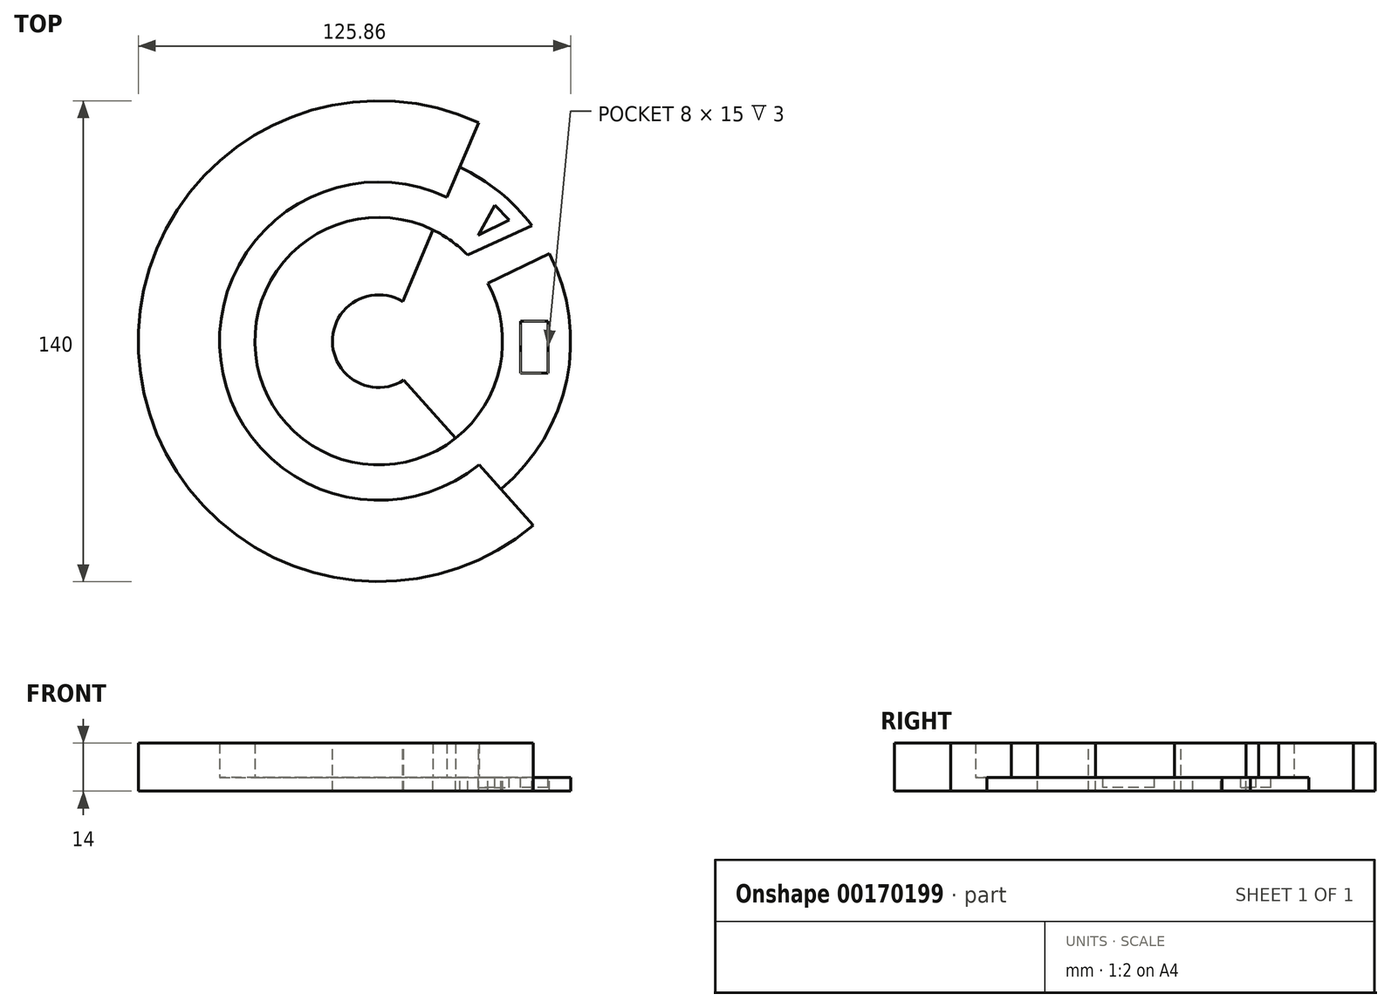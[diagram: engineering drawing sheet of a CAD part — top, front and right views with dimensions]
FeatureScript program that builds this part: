
annotation { "Feature Type Name" : "Feature", "Feature Type Description" : "" }
export const myFeature = defineFeature(function(context is Context, id is Id, definition is map)
    precondition{}
    {
        {
            var Q0;
            Q0=qCreatedBy(makeId("Top.planeOp"),FACE);
            var sketch = newSketch(context, id + "F0", { "sketchPlane" : qUnion([Q0])});
            skCircle(sketch, "E0", {"center": v(0, 0) * mm, "radius": 70 * mm});
            skCircle(sketch, "E1", {"center": v(0, 0) * mm, "radius": 46.34 * mm});
            skCircle(sketch, "E2", {"center": v(0, 0) * mm, "radius": 36.04 * mm});
            skCircle(sketch, "E3", {"center": v(0, 0) * mm, "radius": 13.49 * mm});
            skLineSegment(sketch, "E4", {"start": v(7.26, -11.37) * mm, "end": v(45, -53.62) * mm});
            skLineSegment(sketch, "E5", {"start": v(6.97, 11.55) * mm, "end": v(29.14, 63.65) * mm});
            skCircle(sketch, "E6", {"center": v(0, 0) * mm, "radius": 55.86 * mm});
            skCircle(sketch, "E7", {"center": v(0, 0) * mm, "radius": 32.82 * mm});
            skCircle(sketch, "E8", {"center": v(0, 0) * mm, "radius": 74.95 * mm});
            skLineSegment(sketch, "E9", {"start": v(26.8, -18.95) * mm, "end": v(42.53, -36.22) * mm});
            skLineSegment(sketch, "E10", {"start": v(49.72, 25.46) * mm, "end": v(28.92, 15.51) * mm});
            skLineSegment(sketch, "E11", {"start": v(22.75, 23.65) * mm, "end": v(40.37, 63.15) * mm});
            skLineSegment(sketch, "E12", {"start": v(22.75, 23.65) * mm, "end": v(62.3, 41.68) * mm});
            skSolve(sketch);
        }
        {
            var Q0;
            {var subQ0=sQuery(id+"F0.wireOp",EDGE,"E4");var subQ1=sQuery(id+"F0.wireOp",EDGE,"E0");var subQ2=makeQuery(id+"F0.imprint","INTERSECT",VERTEX,{"derivedFrom":[subQ1,subQ0]});Q0=makeQuery(id+"F0.imprint","IMPRINT",FACE,{"disambiguationData":[TD([[makeQuery(id+"F0.imprint","IMPRINT",EDGE,{"disambiguationData":[TD([[subQ2,1.0]])],"derivedFrom":subQ1}),1.0]])]});}
            var Q1;
            {var subQ0=sQuery(id+"F0.wireOp",EDGE,"E5");var subQ1=sQuery(id+"F0.wireOp",EDGE,"E1");var subQ2=makeQuery(id+"F0.imprint","INTERSECT",VERTEX,{"derivedFrom":[subQ1,subQ0]});Q1=makeQuery(id+"F0.imprint","IMPRINT",FACE,{"disambiguationData":[TD([[makeQuery(id+"F0.imprint","IMPRINT",EDGE,{"disambiguationData":[TD([[subQ2,-1.0]])],"derivedFrom":subQ1}),-1.0]])]});}
            var Q2;
            {var subQ0=sQuery(id+"F0.wireOp",EDGE,"E5");var subQ1=sQuery(id+"F0.wireOp",EDGE,"E2");var subQ2=makeQuery(id+"F0.imprint","INTERSECT",VERTEX,{"derivedFrom":[subQ1,subQ0]});Q2=makeQuery(id+"F0.imprint","IMPRINT",FACE,{"disambiguationData":[TD([[makeQuery(id+"F0.imprint","IMPRINT",EDGE,{"disambiguationData":[TD([[subQ2,-1.0]])],"derivedFrom":subQ1}),1.0]])]});}
            var Q3;
            {var subQ0=sQuery(id+"F0.wireOp",EDGE,"E4");var subQ1=sQuery(id+"F0.wireOp",EDGE,"E3");var subQ2=makeQuery(id+"F0.imprint","INTERSECT",VERTEX,{"derivedFrom":[subQ1,subQ0]});Q3=makeQuery(id+"F0.imprint","IMPRINT",FACE,{"disambiguationData":[TD([[makeQuery(id+"F0.imprint","IMPRINT",EDGE,{"disambiguationData":[TD([[subQ2,1.0]])],"derivedFrom":subQ1}),-1.0]])]});}
            var Q4;
            {var subQ0=sQuery(id+"F0.wireOp",EDGE,"E5");var subQ1=sQuery(id+"F0.wireOp",EDGE,"E1");var subQ2=makeQuery(id+"F0.imprint","INTERSECT",VERTEX,{"derivedFrom":[subQ1,subQ0]});Q4=makeQuery(id+"F0.imprint","IMPRINT",FACE,{"disambiguationData":[TD([[makeQuery(id+"F0.imprint","IMPRINT",EDGE,{"disambiguationData":[TD([[subQ2,-1.0]])],"derivedFrom":subQ1}),1.0]])]});}
            var Q5;
            {var subQ0=sQuery(id+"F0.wireOp",EDGE,"E11");var subQ1=sQuery(id+"F0.wireOp",EDGE,"E1");var subQ2=makeQuery(id+"F0.imprint","INTERSECT",VERTEX,{"derivedFrom":[subQ1,subQ0]});Q5=makeQuery(id+"F0.imprint","IMPRINT",FACE,{"disambiguationData":[TD([[makeQuery(id+"F0.imprint","IMPRINT",EDGE,{"disambiguationData":[TD([[subQ2,-1.0]])],"derivedFrom":subQ1}),-1.0]])]});}
            var Q6;
            {var subQ0=sQuery(id+"F0.wireOp",EDGE,"E11");var subQ1=sQuery(id+"F0.wireOp",EDGE,"E1");var subQ2=makeQuery(id+"F0.imprint","INTERSECT",VERTEX,{"derivedFrom":[subQ1,subQ0]});Q6=makeQuery(id+"F0.imprint","IMPRINT",FACE,{"disambiguationData":[TD([[makeQuery(id+"F0.imprint","IMPRINT",EDGE,{"disambiguationData":[TD([[subQ2,-1.0]])],"derivedFrom":subQ1}),1.0]])]});}
            var Q7;
            {var subQ0=sQuery(id+"F0.wireOp",EDGE,"E12");var subQ1=sQuery(id+"F0.wireOp",EDGE,"E1");var subQ2=makeQuery(id+"F0.imprint","INTERSECT",VERTEX,{"derivedFrom":[subQ1,subQ0]});Q7=makeQuery(id+"F0.imprint","IMPRINT",FACE,{"disambiguationData":[TD([[makeQuery(id+"F0.imprint","IMPRINT",EDGE,{"disambiguationData":[TD([[subQ2,-1.0]])],"derivedFrom":subQ1}),1.0]])]});}
            var Q8;
            {var subQ0=sQuery(id+"F0.wireOp",EDGE,"E12");var subQ1=sQuery(id+"F0.wireOp",EDGE,"E1");var subQ2=makeQuery(id+"F0.imprint","INTERSECT",VERTEX,{"derivedFrom":[subQ1,subQ0]});Q8=makeQuery(id+"F0.imprint","IMPRINT",FACE,{"disambiguationData":[TD([[makeQuery(id+"F0.imprint","IMPRINT",EDGE,{"disambiguationData":[TD([[subQ2,-1.0]])],"derivedFrom":subQ1}),-1.0]])]});}
            var Q9;
            {var subQ0=sQuery(id+"F0.wireOp",EDGE,"E4");var subQ1=sQuery(id+"F0.wireOp",EDGE,"E1");var subQ2=makeQuery(id+"F0.imprint","INTERSECT",VERTEX,{"derivedFrom":[subQ1,subQ0]});Q9=makeQuery(id+"F0.imprint","IMPRINT",FACE,{"disambiguationData":[TD([[makeQuery(id+"F0.imprint","IMPRINT",EDGE,{"disambiguationData":[TD([[subQ2,-1.0]])],"derivedFrom":subQ1}),1.0]])]});}
            var Q10;
            {var subQ0=sQuery(id+"F0.wireOp",EDGE,"E4");var subQ1=sQuery(id+"F0.wireOp",EDGE,"E1");var subQ2=makeQuery(id+"F0.imprint","INTERSECT",VERTEX,{"derivedFrom":[subQ1,subQ0]});Q10=makeQuery(id+"F0.imprint","IMPRINT",FACE,{"disambiguationData":[TD([[makeQuery(id+"F0.imprint","IMPRINT",EDGE,{"disambiguationData":[TD([[subQ2,-1.0]])],"derivedFrom":subQ1}),-1.0]])]});}
            var Q11;
            {var subQ0=sQuery(id+"F0.wireOp",EDGE,"E10");var subQ1=sQuery(id+"F0.wireOp",EDGE,"E1");var subQ2=makeQuery(id+"F0.imprint","INTERSECT",VERTEX,{"derivedFrom":[subQ1,subQ0]});Q11=makeQuery(id+"F0.imprint","IMPRINT",FACE,{"disambiguationData":[TD([[makeQuery(id+"F0.imprint","IMPRINT",EDGE,{"disambiguationData":[TD([[subQ2,1.0]])],"derivedFrom":subQ1}),-1.0]])]});}
            var Q12;
            {var subQ0=sQuery(id+"F0.wireOp",EDGE,"E10");var subQ1=sQuery(id+"F0.wireOp",EDGE,"E1");var subQ2=makeQuery(id+"F0.imprint","INTERSECT",VERTEX,{"derivedFrom":[subQ1,subQ0]});Q12=makeQuery(id+"F0.imprint","IMPRINT",FACE,{"disambiguationData":[TD([[makeQuery(id+"F0.imprint","IMPRINT",EDGE,{"disambiguationData":[TD([[subQ2,1.0]])],"derivedFrom":subQ1}),1.0]])]});}
            extrude(context, id + "F1", {"entities" : qUnion([Q0, Q1, Q2, Q3, Q4, Q5, Q6, Q7, Q8, Q9, Q10, Q11, Q12]), "oppositeDirection" : true, "depth" : 4 * mm});
        }
        {
            var Q0;
            {var subQ0=sQuery(id+"F0.wireOp",EDGE,"E4");var subQ1=sQuery(id+"F0.wireOp",EDGE,"E0");var subQ2=makeQuery(id+"F0.imprint","INTERSECT",VERTEX,{"derivedFrom":[subQ1,subQ0]});Q0=makeQuery(id+"F0.imprint","IMPRINT",FACE,{"disambiguationData":[TD([[makeQuery(id+"F0.imprint","IMPRINT",EDGE,{"disambiguationData":[TD([[subQ2,1.0]])],"derivedFrom":subQ1}),1.0]])]});}
            var Q1;
            {var subQ0=sQuery(id+"F0.wireOp",EDGE,"E5");var subQ1=sQuery(id+"F0.wireOp",EDGE,"E1");var subQ2=makeQuery(id+"F0.imprint","INTERSECT",VERTEX,{"derivedFrom":[subQ1,subQ0]});Q1=makeQuery(id+"F0.imprint","IMPRINT",FACE,{"disambiguationData":[TD([[makeQuery(id+"F0.imprint","IMPRINT",EDGE,{"disambiguationData":[TD([[subQ2,-1.0]])],"derivedFrom":subQ1}),-1.0]])]});}
            var Q2;
            {var subQ0=sQuery(id+"F0.wireOp",EDGE,"E4");var subQ1=sQuery(id+"F0.wireOp",EDGE,"E3");var subQ2=makeQuery(id+"F0.imprint","INTERSECT",VERTEX,{"derivedFrom":[subQ1,subQ0]});Q2=makeQuery(id+"F0.imprint","IMPRINT",FACE,{"disambiguationData":[TD([[makeQuery(id+"F0.imprint","IMPRINT",EDGE,{"disambiguationData":[TD([[subQ2,1.0]])],"derivedFrom":subQ1}),-1.0]])]});}
            var Q3;
            {var subQ0=sQuery(id+"F0.wireOp",EDGE,"E5");var subQ1=sQuery(id+"F0.wireOp",EDGE,"E2");var subQ2=makeQuery(id+"F0.imprint","INTERSECT",VERTEX,{"derivedFrom":[subQ1,subQ0]});Q3=makeQuery(id+"F0.imprint","IMPRINT",FACE,{"disambiguationData":[TD([[makeQuery(id+"F0.imprint","IMPRINT",EDGE,{"disambiguationData":[TD([[subQ2,-1.0]])],"derivedFrom":subQ1}),1.0]])]});}
            extrude(context, id + "F2", {"entities" : qUnion([Q0, Q1, Q2, Q3]), "operationType" : NewBodyOperationType.ADD, "depth" : 10 * mm});
        }
        {
            var Q0;
            {var subQ0=sQuery(id+"F0.wireOp",EDGE,"E12");var subQ1=sQuery(id+"F0.wireOp",EDGE,"E1");var subQ2=makeQuery(id+"F0.imprint","INTERSECT",VERTEX,{"derivedFrom":[subQ1,subQ0]});Q0=makeQuery(id+"F0.imprint","IMPRINT",FACE,{"disambiguationData":[TD([[makeQuery(id+"F0.imprint","IMPRINT",EDGE,{"disambiguationData":[TD([[subQ2,-1.0]])],"derivedFrom":subQ1}),-1.0]])]});}
            var sketch = newSketch(context, id + "F3", { "sketchPlane" : qUnion([Q0])});
            skLineSegment(sketch, "E13", {"start": v(33.85, 39.63) * mm, "end": v(29, 30.88) * mm});
            skLineSegment(sketch, "E14", {"start": v(29, 30.88) * mm, "end": v(37.99, 35.28) * mm});
            skLineSegment(sketch, "E15", {"start": v(33.85, 39.63) * mm, "end": v(37.99, 35.28) * mm});
            skLineSegment(sketch, "E16", {"start": v(41.27, 5.75) * mm, "end": v(41.27, -9.25) * mm});
            skLineSegment(sketch, "E17", {"start": v(41.27, -9.25) * mm, "end": v(49.27, -9.25) * mm});
            skLineSegment(sketch, "E18", {"start": v(49.27, -9.25) * mm, "end": v(49.27, 5.75) * mm});
            skLineSegment(sketch, "E19", {"start": v(49.27, 5.75) * mm, "end": v(41.27, 5.75) * mm});
            skSolve(sketch);
        }
        {
            var Q0;
            Q0=qSketchRegion(id+"F3",true);
            extrude(context, id + "F4", {"entities" : qUnion([Q0]), "operationType" : NewBodyOperationType.REMOVE, "oppositeDirection" : true, "depth" : 3 * mm});
        }
    });
